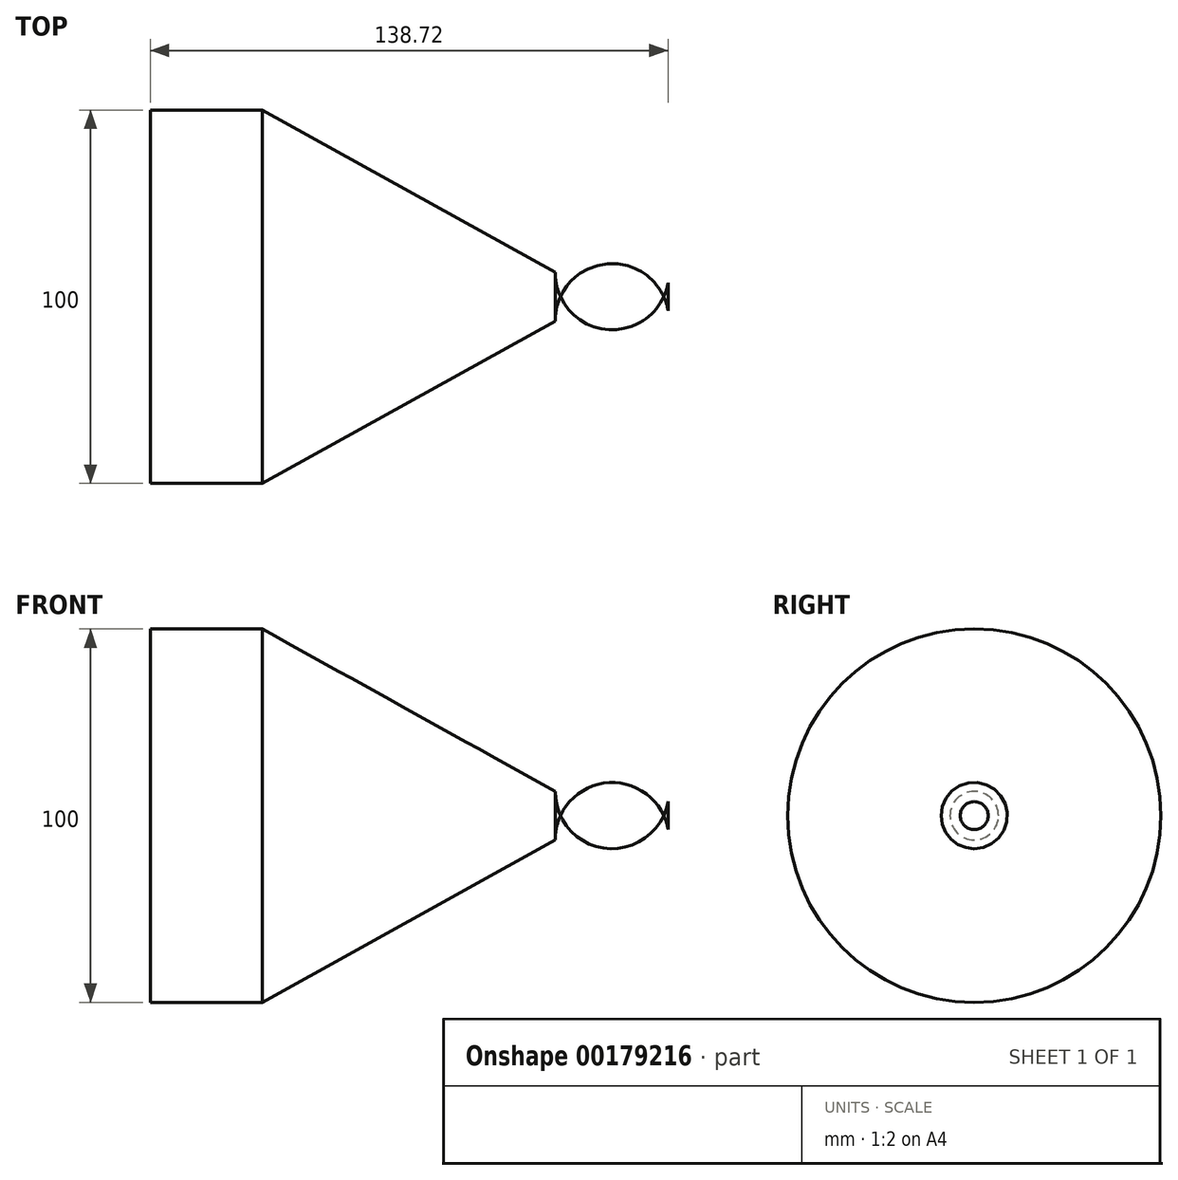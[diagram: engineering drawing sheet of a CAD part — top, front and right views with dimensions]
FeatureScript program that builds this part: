
annotation { "Feature Type Name" : "Feature", "Feature Type Description" : "" }
export const myFeature = defineFeature(function(context is Context, id is Id, definition is map)
    precondition{}
    {
        {
            var Q0;
            Q0=qCreatedBy(makeId("Front.planeOp"),FACE);
            var sketch = newSketch(context, id + "F0", { "sketchPlane" : qUnion([Q0])});
            skLineSegment(sketch, "E0", {"start": v(0, 0) * mm, "end": v(150, 0) * mm, "construction": true});
            skLineSegment(sketch, "E1", {"start": v(0, 0) * mm, "end": v(0, 50) * mm, "construction": true});
            skLineSegment(sketch, "E2", {"start": v(0, 50) * mm, "end": v(30, 50) * mm, "construction": true});
            skLineSegment(sketch, "E3", {"start": v(30, 50) * mm, "end": v(108.72, 6.37) * mm, "construction": true});
            skLineSegment(sketch, "E4", {"start": v(108.72, 6.37) * mm, "end": v(138.72, 6.37) * mm, "construction": true});
            skArc(sketch, "E5", {"start": v(138.72, 3.74) * mm, "mid": v(125.1, 21.53) * mm, "end": v(108.49, 6.5) * mm});
            skLineSegment(sketch, "E6", {"start": v(108.72, 6.37) * mm, "end": v(30, 50) * mm});
            skLineSegment(sketch, "E7", {"start": v(0, 50) * mm, "end": v(0, 0) * mm});
            skLineSegment(sketch, "E8", {"start": v(138.72, 6.37) * mm, "end": v(138.72, 0) * mm});
            skLineSegment(sketch, "E9", {"start": v(138.72, 0) * mm, "end": v(0, 0) * mm});
            skLineSegment(sketch, "E10", {"start": v(0, 50) * mm, "end": v(30, 50) * mm});
            skLineSegment(sketch, "E11", {"start": v(138.94, 6.37) * mm, "end": v(138.94, 0) * mm});
            skSolve(sketch);
        }
        {
            var Q0;
            Q0=makeQuery(id+"F0.imprint","IMPRINT",FACE,{"disambiguationData":[TD([[makeQuery(id+"F0.imprint","IMPRINT",EDGE,{"derivedFrom":sQuery(id+"F0.wireOp",EDGE,"E7")}),1.0]])]});
            var Q1;
            Q1=sQuery(id+"F0.wireOp",EDGE,"E0");
            revolve(context, id + "F1", {"entities" : qUnion([Q0]), "axis" : qUnion([Q1]), "revolveType" : RevolveType.FULL});
        }
    });
